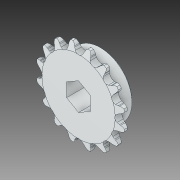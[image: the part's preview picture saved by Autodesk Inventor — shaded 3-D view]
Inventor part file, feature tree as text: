
AUTODESK INVENTOR PART (.ipt)
format: ipt  version: 2019 (Build 230136000, 136)  size: 460,800 bytes
history: native  units: in
note: dims shown in document units (in); Inventor stores cm internally (conversion verified against a paired STEP export)
features: chamfer x1
ambient origin geometry x8: Origin, YZ Plane, XZ Plane, XY Plane, X Axis, Y Axis, Z Axis, Center Point
bodies: Solid1 (feature_tree)
feature tree (1):
  chamfer  "Chamfer2"  [1 undecoded]
note: 1 required parameter value undecoded (feature->parameter linkage not recoverable at this tier; creation-order binding heuristic only, values carry confidence <= 0.55)
